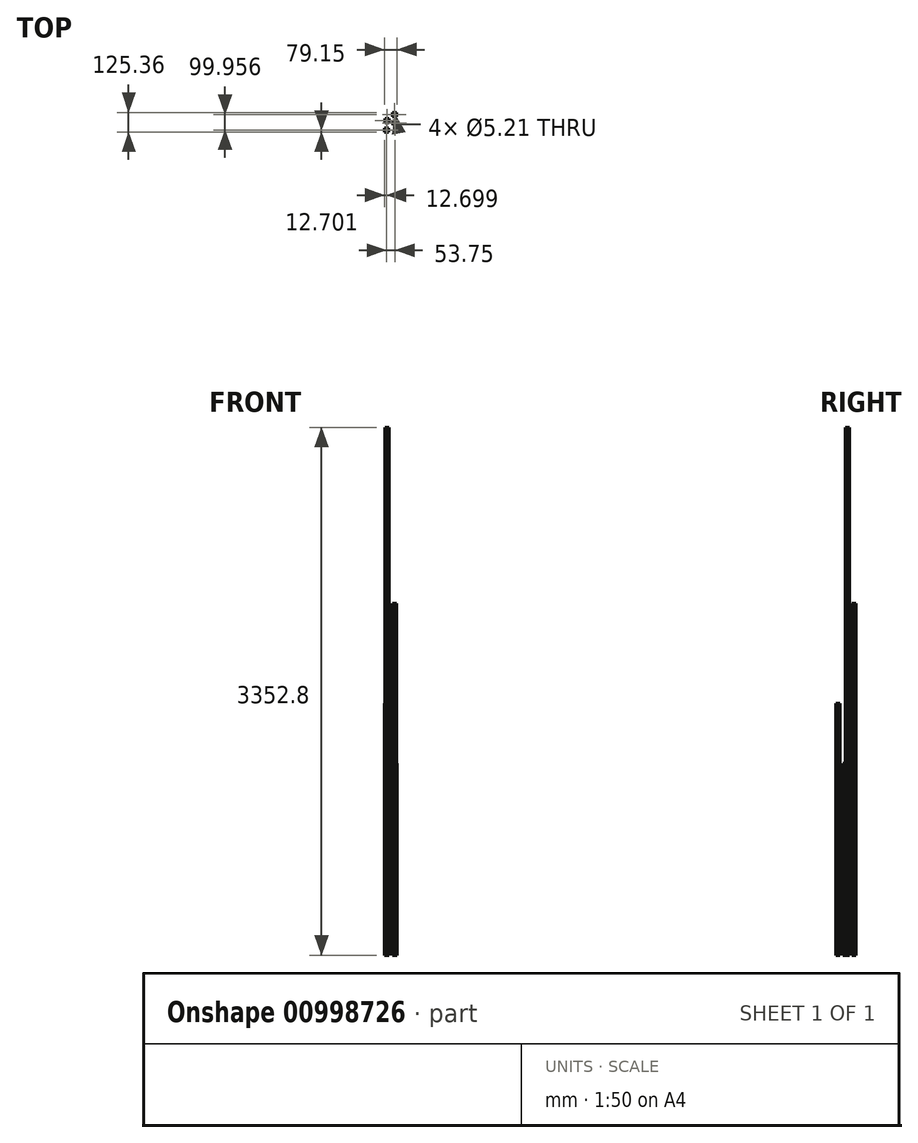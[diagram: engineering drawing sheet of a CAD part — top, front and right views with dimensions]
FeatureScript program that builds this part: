
annotation { "Feature Type Name" : "Feature", "Feature Type Description" : "" }
export const myFeature = defineFeature(function(context is Context, id is Id, definition is map)
    precondition{}
    {
        {
            var Q0;
            Q0=qCreatedBy(makeId("Front.planeOp"),FACE);
            var sketch = newSketch(context, id + "F0", { "sketchPlane" : qUnion([Q0])});
            skLineSegment(sketch, "E0.bottom", {"start": v(-114.36, 2066.6) * mm, "end": v(-88.96, 2066.6) * mm});
            skLineSegment(sketch, "E0.top", {"start": v(-114.36, -168.6) * mm, "end": v(-88.96, -168.6) * mm});
            skLineSegment(sketch, "E0.left", {"start": v(-114.36, 2066.6) * mm, "end": v(-114.36, -168.6) * mm});
            skLineSegment(sketch, "E0.right", {"start": v(-88.96, 2066.6) * mm, "end": v(-88.96, -168.6) * mm});
            skSolve(sketch);
        }
        {
            var Q0;
            Q0=makeQuery(id+"F0.imprint","IMPRINT",FACE,{"disambiguationData":[TD([[makeQuery(id+"F0.imprint","IMPRINT",EDGE,{"derivedFrom":sQuery(id+"F0.wireOp",EDGE,"E0.bottom")}),-1.0]])]});
            extrude(context, id + "F1", {"entities" : qUnion([Q0]), "depth" : 25.4 * mm, "offsetDistance" : 25.4 * mm});
        }
        {
            var Q0;
            Q0=qCreatedBy(makeId("Top.planeOp"),FACE);
            var sketch = newSketch(context, id + "F2", { "sketchPlane" : qUnion([Q0])});
            skLineSegment(sketch, "E1.bottom", {"start": v(-14.47, 19.18) * mm, "end": v(10.93, 19.18) * mm});
            skLineSegment(sketch, "E1.top", {"start": v(-14.47, -6.22) * mm, "end": v(10.93, -6.22) * mm});
            skLineSegment(sketch, "E1.left", {"start": v(-14.47, 19.18) * mm, "end": v(-14.47, -6.22) * mm});
            skLineSegment(sketch, "E1.right", {"start": v(10.93, 19.18) * mm, "end": v(10.93, -6.22) * mm});
            skPoint(sketch, "E2", {"position": v(-1.77, 19.18) * mm});
            skPoint(sketch, "E3", {"position": v(-14.47, 6.48) * mm});
            skSolve(sketch);
        }
        {
            var Q0;
            Q0=qCreatedBy(makeId("Top.planeOp"),FACE);
            var sketch = newSketch(context, id + "F3", { "sketchPlane" : qUnion([Q0])});
            skLineSegment(sketch, "E4.bottom", {"start": v(-5.02, 19.18) * mm, "end": v(1.48, 19.18) * mm});
            skLineSegment(sketch, "E4.top", {"start": v(-2.48, 10.97) * mm, "end": v(-1.06, 10.97) * mm});
            skLineSegment(sketch, "E4.left", {"start": v(-5.02, 19.18) * mm, "end": v(-5.02, 13.51) * mm});
            skLineSegment(sketch, "E4.right", {"start": v(1.48, 19.18) * mm, "end": v(1.48, 13.51) * mm});
            skLineSegment(sketch, "E5.MirrorCS", {"start": v(-5.02, -6.22) * mm, "end": v(1.48, -6.22) * mm});
            skLineSegment(sketch, "E6.MirrorCS", {"start": v(-5.02, -6.22) * mm, "end": v(-5.02, -0.56) * mm});
            skLineSegment(sketch, "E7.MirrorCS", {"start": v(-2.48, 1.98) * mm, "end": v(-1.06, 1.98) * mm});
            skLineSegment(sketch, "E8.MirrorCS", {"start": v(1.48, -6.22) * mm, "end": v(1.48, -0.56) * mm});
            skLineSegment(sketch, "E9.bottom", {"start": v(-14.47, 9.73) * mm, "end": v(-8.8, 9.73) * mm});
            skLineSegment(sketch, "E9.top", {"start": v(-14.47, 3.23) * mm, "end": v(-8.8, 3.23) * mm});
            skLineSegment(sketch, "E9.left", {"start": v(-14.47, 9.73) * mm, "end": v(-14.47, 3.23) * mm});
            skLineSegment(sketch, "E9.right", {"start": v(-6.26, 7.19) * mm, "end": v(-6.26, 5.77) * mm});
            skLineSegment(sketch, "E10.MirrorCS", {"start": v(10.93, 9.73) * mm, "end": v(5.27, 9.73) * mm});
            skLineSegment(sketch, "E11.MirrorCS", {"start": v(10.93, 9.73) * mm, "end": v(10.93, 3.23) * mm});
            skLineSegment(sketch, "E12.MirrorCS", {"start": v(10.93, 3.23) * mm, "end": v(5.27, 3.23) * mm});
            skLineSegment(sketch, "E13.MirrorCS", {"start": v(2.73, 7.19) * mm, "end": v(2.73, 5.77) * mm});
            skPoint(sketch, "E14.visualSharp", {"position": v(-5.02, 1.98) * mm});
            skArc(sketch, "E14.filletArc", {"start": v(-2.48, 1.98) * mm, "mid": v(-4.27, 1.24) * mm, "end": v(-5.02, -0.56) * mm});
            skPoint(sketch, "E15.visualSharp", {"position": v(1.48, 1.98) * mm});
            skArc(sketch, "E15.filletArc", {"start": v(1.48, -0.56) * mm, "mid": v(0.74, 1.24) * mm, "end": v(-1.06, 1.98) * mm});
            skPoint(sketch, "E16.visualSharp", {"position": v(-6.26, 3.23) * mm});
            skArc(sketch, "E16.filletArc", {"start": v(-8.8, 3.23) * mm, "mid": v(-7, 3.97) * mm, "end": v(-6.26, 5.77) * mm});
            skPoint(sketch, "E17.visualSharp", {"position": v(-6.26, 9.73) * mm});
            skArc(sketch, "E17.filletArc", {"start": v(-6.26, 7.19) * mm, "mid": v(-7, 8.98) * mm, "end": v(-8.8, 9.73) * mm});
            skPoint(sketch, "E18.visualSharp", {"position": v(2.73, 3.23) * mm});
            skArc(sketch, "E18.filletArc", {"start": v(2.73, 5.77) * mm, "mid": v(3.47, 3.97) * mm, "end": v(5.27, 3.23) * mm});
            skPoint(sketch, "E19.visualSharp", {"position": v(2.73, 9.73) * mm});
            skArc(sketch, "E19.filletArc", {"start": v(5.27, 9.73) * mm, "mid": v(3.47, 8.98) * mm, "end": v(2.73, 7.19) * mm});
            skPoint(sketch, "E20.visualSharp", {"position": v(-5.02, 10.97) * mm});
            skArc(sketch, "E20.filletArc", {"start": v(-5.02, 13.51) * mm, "mid": v(-4.27, 11.72) * mm, "end": v(-2.48, 10.97) * mm});
            skPoint(sketch, "E21.visualSharp", {"position": v(1.48, 10.97) * mm});
            skArc(sketch, "E21.filletArc", {"start": v(-1.06, 10.97) * mm, "mid": v(0.74, 11.72) * mm, "end": v(1.48, 13.51) * mm});
            skCircle(sketch, "E22", {"center": v(-1.77, 6.48) * mm, "radius": 2.6 * mm});
            skPoint(sketch, "E22.centerSnap0", {"position": v(-6.26, 6.48) * mm});
            skPoint(sketch, "E22.centerSnap1", {"position": v(-1.77, 10.97) * mm});
            skSolve(sketch);
        }
        {
            var Q0;
            Q0=makeQuery(id+"F2.imprint","IMPRINT",FACE,{"disambiguationData":[TD([[makeQuery(id+"F2.imprint","IMPRINT",EDGE,{"derivedFrom":sQuery(id+"F2.wireOp",EDGE,"E1.bottom")}),-1.0]])]});
            extrude(context, id + "F4", {"entities" : qUnion([Q0]), "depth" : 2235.2 * mm, "offsetDistance" : 25.4 * mm});
        }
        {
            var Q0;
            Q0 = qSketchRegion(id + "F3", true);
            extrude(context, id + "F5", {"entities" : qUnion([Q0]), "operationType" : NewBodyOperationType.REMOVE, "depth" : 2235.2 * mm, "offsetDistance" : 25.4 * mm});
        }
        {
            var Q0;
            Q0=makeQuery(id+"F1.opExtrude","SWEPT_BODY",BODY,{"disambiguationData":[OSD([sQuery(id+"F0.wireOp",EDGE,"E0.bottom"),sQuery(id+"F0.wireOp",EDGE,"E0.top"),sQuery(id+"F0.wireOp",EDGE,"E0.left"),sQuery(id+"F0.wireOp",EDGE,"E0.right")])]});
            deleteBodies(context, id + "F6", {"entities" : qUnion([Q0])});
        }
        {
            var Q0;
            Q0=makeQuery(id+"F4.opExtrude","SWEPT_BODY",BODY,{"disambiguationData":[OSD([sQuery(id+"F2.wireOp",EDGE,"E1.bottom"),sQuery(id+"F2.wireOp",EDGE,"E1.top"),sQuery(id+"F2.wireOp",EDGE,"E1.left"),sQuery(id+"F2.wireOp",EDGE,"E1.right")])]});
            var Q1;
            Q1=qCreatedBy(makeId("Front.planeOp"),FACE);
            mirror(context, id + "F7", {"entities" : qUnion([Q0]), "mirrorPlane" : qUnion([Q1])});
        }
        {
            var Q0;
            Q0=makeQuery(id+"F4.opExtrude","SWEPT_BODY",BODY,{"disambiguationData":[OSD([sQuery(id+"F2.wireOp",EDGE,"E1.bottom"),sQuery(id+"F2.wireOp",EDGE,"E1.top"),sQuery(id+"F2.wireOp",EDGE,"E1.left"),sQuery(id+"F2.wireOp",EDGE,"E1.right")])]});
            var Q1;
            Q1=makeQuery(id+"F5.boolean.opBoolean","COPY",EDGE,{"derivedFrom":makeQuery(id+"F5.opExtrude","SWEPT_EDGE",EDGE,{"disambiguationData":[OSD([sQuery(id+"F3.wireOp",EDGE,"E4.left"),sQuery(id+"F3.wireOp",EDGE,"E20.filletArc")])]})});
            transform(context, id + "F8", {"entities" : qUnion([Q0]), "transformType" : TransformType.TRANSLATION_3D, "dx" : 0 * mm, "dy" : 17.78 * mm, "dz" : 0 * mm, "makeCopy" : false});
        }
        {
            var Q0;
            Q0=makeQuery(id+"F4.opExtrude","SWEPT_BODY",BODY,{"disambiguationData":[OSD([sQuery(id+"F2.wireOp",EDGE,"E1.bottom"),sQuery(id+"F2.wireOp",EDGE,"E1.top"),sQuery(id+"F2.wireOp",EDGE,"E1.left"),sQuery(id+"F2.wireOp",EDGE,"E1.right")])]});
            transform(context, id + "F9", {"entities" : qUnion([Q0]), "transformType" : TransformType.TRANSLATION_3D, "dx" : 0 * mm, "dy" : 31.75 * mm, "dz" : 0 * mm, "makeCopy" : false});
        }
        {
            var Q0;
            Q0=makeQuery(id+"F7.opPattern","COPY",BODY,{"derivedFrom":makeQuery(id+"F4.opExtrude","SWEPT_BODY",BODY,{"disambiguationData":[OSD([sQuery(id+"F2.wireOp",EDGE,"E1.bottom"),sQuery(id+"F2.wireOp",EDGE,"E1.top"),sQuery(id+"F2.wireOp",EDGE,"E1.left"),sQuery(id+"F2.wireOp",EDGE,"E1.right")])]}),"instanceName":"1"});
            deleteBodies(context, id + "F10", {"entities" : qUnion([Q0])});
        }
        {
            var Q0;
            Q0=qCreatedBy(makeId("Top.planeOp"),FACE);
            var sketch = newSketch(context, id + "F11", { "sketchPlane" : qUnion([Q0])});
            skLineSegment(sketch, "E23.bottom", {"start": v(-12.57, 12.57) * mm, "end": v(12.83, 12.57) * mm});
            skLineSegment(sketch, "E23.top", {"start": v(-12.57, -12.83) * mm, "end": v(12.83, -12.83) * mm});
            skLineSegment(sketch, "E23.left", {"start": v(-12.57, 12.57) * mm, "end": v(-12.57, -12.83) * mm});
            skLineSegment(sketch, "E23.right", {"start": v(12.83, 12.57) * mm, "end": v(12.83, -12.83) * mm});
            skPoint(sketch, "E24", {"position": v(0.13, 12.57) * mm});
            skPoint(sketch, "E25", {"position": v(-12.57, -0.13) * mm});
            skLineSegment(sketch, "E26.bottom", {"start": v(-3.12, 12.57) * mm, "end": v(3.38, 12.57) * mm});
            skLineSegment(sketch, "E26.top", {"start": v(-0.58, 4.37) * mm, "end": v(0.84, 4.37) * mm});
            skLineSegment(sketch, "E26.left", {"start": v(-3.12, 12.57) * mm, "end": v(-3.12, 6.9) * mm});
            skLineSegment(sketch, "E26.right", {"start": v(3.38, 12.57) * mm, "end": v(3.38, 6.9) * mm});
            skLineSegment(sketch, "E27.MirrorCS", {"start": v(-3.12, -12.83) * mm, "end": v(3.38, -12.83) * mm});
            skLineSegment(sketch, "E28.MirrorCS", {"start": v(-3.12, -12.83) * mm, "end": v(-3.12, -7.16) * mm});
            skLineSegment(sketch, "E29.MirrorCS", {"start": v(-0.58, -4.62) * mm, "end": v(0.84, -4.62) * mm});
            skLineSegment(sketch, "E30.MirrorCS", {"start": v(3.38, -12.83) * mm, "end": v(3.38, -7.16) * mm});
            skLineSegment(sketch, "E31.bottom", {"start": v(-12.57, 3.12) * mm, "end": v(-6.9, 3.12) * mm});
            skLineSegment(sketch, "E31.top", {"start": v(-12.57, -3.38) * mm, "end": v(-6.9, -3.38) * mm});
            skLineSegment(sketch, "E31.left", {"start": v(-12.57, 3.12) * mm, "end": v(-12.57, -3.38) * mm});
            skLineSegment(sketch, "E31.right", {"start": v(-4.37, 0.58) * mm, "end": v(-4.37, -0.84) * mm});
            skLineSegment(sketch, "E32.MirrorCS", {"start": v(12.83, 3.12) * mm, "end": v(7.16, 3.12) * mm});
            skLineSegment(sketch, "E33.MirrorCS", {"start": v(12.83, 3.12) * mm, "end": v(12.83, -3.38) * mm});
            skLineSegment(sketch, "E34.MirrorCS", {"start": v(12.83, -3.38) * mm, "end": v(7.16, -3.38) * mm});
            skLineSegment(sketch, "E35.MirrorCS", {"start": v(4.62, 0.58) * mm, "end": v(4.62, -0.84) * mm});
            skPoint(sketch, "E36.visualSharp", {"position": v(-3.12, -4.62) * mm});
            skArc(sketch, "E36.filletArc", {"start": v(-0.58, -4.62) * mm, "mid": v(-2.38, -5.37) * mm, "end": v(-3.12, -7.16) * mm});
            skPoint(sketch, "E37.visualSharp", {"position": v(3.38, -4.62) * mm});
            skArc(sketch, "E37.filletArc", {"start": v(3.38, -7.16) * mm, "mid": v(2.64, -5.37) * mm, "end": v(0.84, -4.62) * mm});
            skPoint(sketch, "E38.visualSharp", {"position": v(-4.37, -3.38) * mm});
            skArc(sketch, "E38.filletArc", {"start": v(-6.9, -3.38) * mm, "mid": v(-5.11, -2.64) * mm, "end": v(-4.37, -0.84) * mm});
            skPoint(sketch, "E39.visualSharp", {"position": v(-4.37, 3.12) * mm});
            skArc(sketch, "E39.filletArc", {"start": v(-4.37, 0.58) * mm, "mid": v(-5.11, 2.38) * mm, "end": v(-6.9, 3.12) * mm});
            skPoint(sketch, "E40.visualSharp", {"position": v(4.62, -3.38) * mm});
            skArc(sketch, "E40.filletArc", {"start": v(4.62, -0.84) * mm, "mid": v(5.37, -2.64) * mm, "end": v(7.16, -3.38) * mm});
            skPoint(sketch, "E41.visualSharp", {"position": v(4.62, 3.12) * mm});
            skArc(sketch, "E41.filletArc", {"start": v(7.16, 3.12) * mm, "mid": v(5.37, 2.38) * mm, "end": v(4.62, 0.58) * mm});
            skPoint(sketch, "E42.visualSharp", {"position": v(-3.12, 4.37) * mm});
            skArc(sketch, "E42.filletArc", {"start": v(-3.12, 6.9) * mm, "mid": v(-2.38, 5.11) * mm, "end": v(-0.58, 4.37) * mm});
            skPoint(sketch, "E43.visualSharp", {"position": v(3.38, 4.37) * mm});
            skArc(sketch, "E43.filletArc", {"start": v(0.84, 4.37) * mm, "mid": v(2.64, 5.11) * mm, "end": v(3.38, 6.9) * mm});
            skCircle(sketch, "E44", {"center": v(0.13, -0.13) * mm, "radius": 2.6 * mm});
            skPoint(sketch, "E44.centerSnap0", {"position": v(-4.37, -0.13) * mm});
            skPoint(sketch, "E44.centerSnap1", {"position": v(0.13, 4.37) * mm});
            skSolve(sketch);
        }
        {
            var Q0;
            Q0=makeQuery(id+"F11.imprint","IMPRINT",FACE,{"disambiguationData":[TD([[makeQuery(id+"F11.imprint","IMPRINT",EDGE,{"derivedFrom":sQuery(id+"F11.wireOp",EDGE,"E26.top")}),-1.0]])]});
            extrude(context, id + "F12", {"entities" : qUnion([Q0]), "depth" : 1219.2 * mm, "offsetDistance" : 25.4 * mm});
        }
        {
            var Q0;
            Q0=qCreatedBy(makeId("Top.planeOp"),FACE);
            var sketch = newSketch(context, id + "F13", { "sketchPlane" : qUnion([Q0])});
            skLineSegment(sketch, "E45.bottom", {"start": v(-61.87, 29.84) * mm, "end": v(-36.47, 29.84) * mm});
            skLineSegment(sketch, "E45.top", {"start": v(-61.87, 4.44) * mm, "end": v(-36.47, 4.44) * mm});
            skLineSegment(sketch, "E45.left", {"start": v(-61.87, 29.84) * mm, "end": v(-61.87, 4.44) * mm});
            skLineSegment(sketch, "E45.right", {"start": v(-36.47, 29.84) * mm, "end": v(-36.47, 4.44) * mm});
            skPoint(sketch, "E46", {"position": v(-49.17, 29.84) * mm});
            skPoint(sketch, "E47", {"position": v(-61.87, 17.14) * mm});
            skLineSegment(sketch, "E48.bottom", {"start": v(-52.42, 29.84) * mm, "end": v(-45.92, 29.84) * mm});
            skLineSegment(sketch, "E48.top", {"start": v(-49.88, 21.64) * mm, "end": v(-48.46, 21.64) * mm});
            skLineSegment(sketch, "E48.left", {"start": v(-52.42, 29.84) * mm, "end": v(-52.42, 24.18) * mm});
            skLineSegment(sketch, "E48.right", {"start": v(-45.92, 29.84) * mm, "end": v(-45.92, 24.18) * mm});
            skLineSegment(sketch, "E49.MirrorCS", {"start": v(-52.42, 4.44) * mm, "end": v(-45.92, 4.44) * mm});
            skLineSegment(sketch, "E50.MirrorCS", {"start": v(-52.42, 4.44) * mm, "end": v(-52.42, 10.1) * mm});
            skLineSegment(sketch, "E51.MirrorCS", {"start": v(-49.88, 12.64) * mm, "end": v(-48.46, 12.64) * mm});
            skLineSegment(sketch, "E52.MirrorCS", {"start": v(-45.92, 4.44) * mm, "end": v(-45.92, 10.1) * mm});
            skLineSegment(sketch, "E53.bottom", {"start": v(-61.87, 20.4) * mm, "end": v(-56.2, 20.4) * mm});
            skLineSegment(sketch, "E53.top", {"start": v(-61.87, 13.89) * mm, "end": v(-56.2, 13.89) * mm});
            skLineSegment(sketch, "E53.left", {"start": v(-61.87, 20.4) * mm, "end": v(-61.87, 13.89) * mm});
            skLineSegment(sketch, "E53.right", {"start": v(-53.67, 17.85) * mm, "end": v(-53.67, 16.43) * mm});
            skLineSegment(sketch, "E54.MirrorCS", {"start": v(-36.47, 20.4) * mm, "end": v(-42.13, 20.4) * mm});
            skLineSegment(sketch, "E55.MirrorCS", {"start": v(-36.47, 20.4) * mm, "end": v(-36.47, 13.89) * mm});
            skLineSegment(sketch, "E56.MirrorCS", {"start": v(-36.47, 13.89) * mm, "end": v(-42.13, 13.89) * mm});
            skLineSegment(sketch, "E57.MirrorCS", {"start": v(-44.67, 17.85) * mm, "end": v(-44.67, 16.43) * mm});
            skPoint(sketch, "E58.visualSharp", {"position": v(-52.42, 12.64) * mm});
            skArc(sketch, "E58.filletArc", {"start": v(-49.88, 12.64) * mm, "mid": v(-51.68, 11.9) * mm, "end": v(-52.42, 10.1) * mm});
            skPoint(sketch, "E59.visualSharp", {"position": v(-45.92, 12.64) * mm});
            skArc(sketch, "E59.filletArc", {"start": v(-45.92, 10.1) * mm, "mid": v(-46.66, 11.9) * mm, "end": v(-48.46, 12.64) * mm});
            skPoint(sketch, "E60.visualSharp", {"position": v(-53.67, 13.89) * mm});
            skArc(sketch, "E60.filletArc", {"start": v(-56.2, 13.89) * mm, "mid": v(-54.4, 14.63) * mm, "end": v(-53.67, 16.43) * mm});
            skPoint(sketch, "E61.visualSharp", {"position": v(-53.67, 20.4) * mm});
            skArc(sketch, "E61.filletArc", {"start": v(-53.67, 17.85) * mm, "mid": v(-54.4, 19.65) * mm, "end": v(-56.2, 20.4) * mm});
            skPoint(sketch, "E62.visualSharp", {"position": v(-44.67, 13.89) * mm});
            skArc(sketch, "E62.filletArc", {"start": v(-44.67, 16.43) * mm, "mid": v(-43.93, 14.63) * mm, "end": v(-42.13, 13.89) * mm});
            skPoint(sketch, "E63.visualSharp", {"position": v(-44.67, 20.4) * mm});
            skArc(sketch, "E63.filletArc", {"start": v(-42.13, 20.4) * mm, "mid": v(-43.93, 19.65) * mm, "end": v(-44.67, 17.85) * mm});
            skPoint(sketch, "E64.visualSharp", {"position": v(-52.42, 21.64) * mm});
            skArc(sketch, "E64.filletArc", {"start": v(-52.42, 24.18) * mm, "mid": v(-51.68, 22.38) * mm, "end": v(-49.88, 21.64) * mm});
            skPoint(sketch, "E65.visualSharp", {"position": v(-45.92, 21.64) * mm});
            skArc(sketch, "E65.filletArc", {"start": v(-48.46, 21.64) * mm, "mid": v(-46.66, 22.38) * mm, "end": v(-45.92, 24.18) * mm});
            skCircle(sketch, "E66", {"center": v(-49.17, 17.14) * mm, "radius": 2.6 * mm});
            skPoint(sketch, "E66.centerSnap0", {"position": v(-53.67, 17.14) * mm});
            skPoint(sketch, "E66.centerSnap1", {"position": v(-49.17, 21.64) * mm});
            skSolve(sketch);
        }
        {
            var Q0;
            Q0=makeQuery(id+"F13.imprint","IMPRINT",FACE,{"disambiguationData":[TD([[makeQuery(id+"F13.imprint","IMPRINT",EDGE,{"derivedFrom":sQuery(id+"F13.wireOp",EDGE,"E48.top")}),-1.0]])]});
            extrude(context, id + "F14", {"entities" : qUnion([Q0]), "depth" : 3352.8 * mm, "offsetDistance" : 25.4 * mm});
        }
        {
            var Q0;
            Q0=qCreatedBy(makeId("Top.planeOp"),FACE);
            var sketch = newSketch(context, id + "F15", { "sketchPlane" : qUnion([Q0])});
            skLineSegment(sketch, "E67.bottom", {"start": v(-66.32, -31.25) * mm, "end": v(-40.92, -31.25) * mm});
            skLineSegment(sketch, "E67.top", {"start": v(-66.32, -56.65) * mm, "end": v(-40.92, -56.65) * mm});
            skLineSegment(sketch, "E67.left", {"start": v(-66.32, -31.25) * mm, "end": v(-66.32, -56.65) * mm});
            skLineSegment(sketch, "E67.right", {"start": v(-40.92, -31.25) * mm, "end": v(-40.92, -56.65) * mm});
            skPoint(sketch, "E68", {"position": v(-53.62, -31.25) * mm});
            skPoint(sketch, "E69", {"position": v(-66.32, -43.95) * mm});
            skLineSegment(sketch, "E70.bottom", {"start": v(-56.87, -31.25) * mm, "end": v(-50.37, -31.25) * mm});
            skLineSegment(sketch, "E70.top", {"start": v(-54.33, -39.45) * mm, "end": v(-52.91, -39.45) * mm});
            skLineSegment(sketch, "E70.left", {"start": v(-56.87, -31.25) * mm, "end": v(-56.87, -36.91) * mm});
            skLineSegment(sketch, "E70.right", {"start": v(-50.37, -31.25) * mm, "end": v(-50.37, -36.91) * mm});
            skLineSegment(sketch, "E71.MirrorCS", {"start": v(-56.87, -56.65) * mm, "end": v(-50.37, -56.65) * mm});
            skLineSegment(sketch, "E72.MirrorCS", {"start": v(-56.87, -56.65) * mm, "end": v(-56.87, -50.98) * mm});
            skLineSegment(sketch, "E73.MirrorCS", {"start": v(-54.33, -48.44) * mm, "end": v(-52.91, -48.44) * mm});
            skLineSegment(sketch, "E74.MirrorCS", {"start": v(-50.37, -56.65) * mm, "end": v(-50.37, -50.98) * mm});
            skLineSegment(sketch, "E75.bottom", {"start": v(-66.32, -40.7) * mm, "end": v(-60.66, -40.7) * mm});
            skLineSegment(sketch, "E75.top", {"start": v(-66.32, -47.2) * mm, "end": v(-60.66, -47.2) * mm});
            skLineSegment(sketch, "E75.left", {"start": v(-66.32, -40.7) * mm, "end": v(-66.32, -47.2) * mm});
            skLineSegment(sketch, "E75.right", {"start": v(-58.12, -43.24) * mm, "end": v(-58.12, -44.66) * mm});
            skLineSegment(sketch, "E76.MirrorCS", {"start": v(-40.92, -40.7) * mm, "end": v(-46.59, -40.7) * mm});
            skLineSegment(sketch, "E77.MirrorCS", {"start": v(-40.92, -40.7) * mm, "end": v(-40.92, -47.2) * mm});
            skLineSegment(sketch, "E78.MirrorCS", {"start": v(-40.92, -47.2) * mm, "end": v(-46.59, -47.2) * mm});
            skLineSegment(sketch, "E79.MirrorCS", {"start": v(-49.13, -43.24) * mm, "end": v(-49.13, -44.66) * mm});
            skPoint(sketch, "E80.visualSharp", {"position": v(-56.87, -48.44) * mm});
            skArc(sketch, "E80.filletArc", {"start": v(-54.33, -48.44) * mm, "mid": v(-56.13, -49.19) * mm, "end": v(-56.87, -50.98) * mm});
            skPoint(sketch, "E81.visualSharp", {"position": v(-50.37, -48.44) * mm});
            skArc(sketch, "E81.filletArc", {"start": v(-50.37, -50.98) * mm, "mid": v(-51.11, -49.19) * mm, "end": v(-52.91, -48.44) * mm});
            skPoint(sketch, "E82.visualSharp", {"position": v(-58.12, -47.2) * mm});
            skArc(sketch, "E82.filletArc", {"start": v(-60.66, -47.2) * mm, "mid": v(-58.86, -46.46) * mm, "end": v(-58.12, -44.66) * mm});
            skPoint(sketch, "E83.visualSharp", {"position": v(-58.12, -40.7) * mm});
            skArc(sketch, "E83.filletArc", {"start": v(-58.12, -43.24) * mm, "mid": v(-58.86, -41.44) * mm, "end": v(-60.66, -40.7) * mm});
            skPoint(sketch, "E84.visualSharp", {"position": v(-49.13, -47.2) * mm});
            skArc(sketch, "E84.filletArc", {"start": v(-49.13, -44.66) * mm, "mid": v(-48.38, -46.46) * mm, "end": v(-46.59, -47.2) * mm});
            skPoint(sketch, "E85.visualSharp", {"position": v(-49.13, -40.7) * mm});
            skArc(sketch, "E85.filletArc", {"start": v(-46.59, -40.7) * mm, "mid": v(-48.38, -41.44) * mm, "end": v(-49.13, -43.24) * mm});
            skPoint(sketch, "E86.visualSharp", {"position": v(-56.87, -39.45) * mm});
            skArc(sketch, "E86.filletArc", {"start": v(-56.87, -36.91) * mm, "mid": v(-56.13, -38.7) * mm, "end": v(-54.33, -39.45) * mm});
            skPoint(sketch, "E87.visualSharp", {"position": v(-50.37, -39.45) * mm});
            skArc(sketch, "E87.filletArc", {"start": v(-52.91, -39.45) * mm, "mid": v(-51.11, -38.7) * mm, "end": v(-50.37, -36.91) * mm});
            skCircle(sketch, "E88", {"center": v(-53.62, -43.95) * mm, "radius": 2.6 * mm});
            skPoint(sketch, "E88.centerSnap0", {"position": v(-58.12, -43.95) * mm});
            skPoint(sketch, "E88.centerSnap1", {"position": v(-53.62, -39.45) * mm});
            skSolve(sketch);
        }
        {
            var Q0;
            Q0=makeQuery(id+"F15.imprint","IMPRINT",FACE,{"disambiguationData":[TD([[makeQuery(id+"F15.imprint","IMPRINT",EDGE,{"derivedFrom":sQuery(id+"F15.wireOp",EDGE,"E70.top")}),-1.0]])]});
            extrude(context, id + "F16", {"entities" : qUnion([Q0]), "depth" : 1600.2 * mm, "offsetDistance" : 25.4 * mm});
        }
    });
